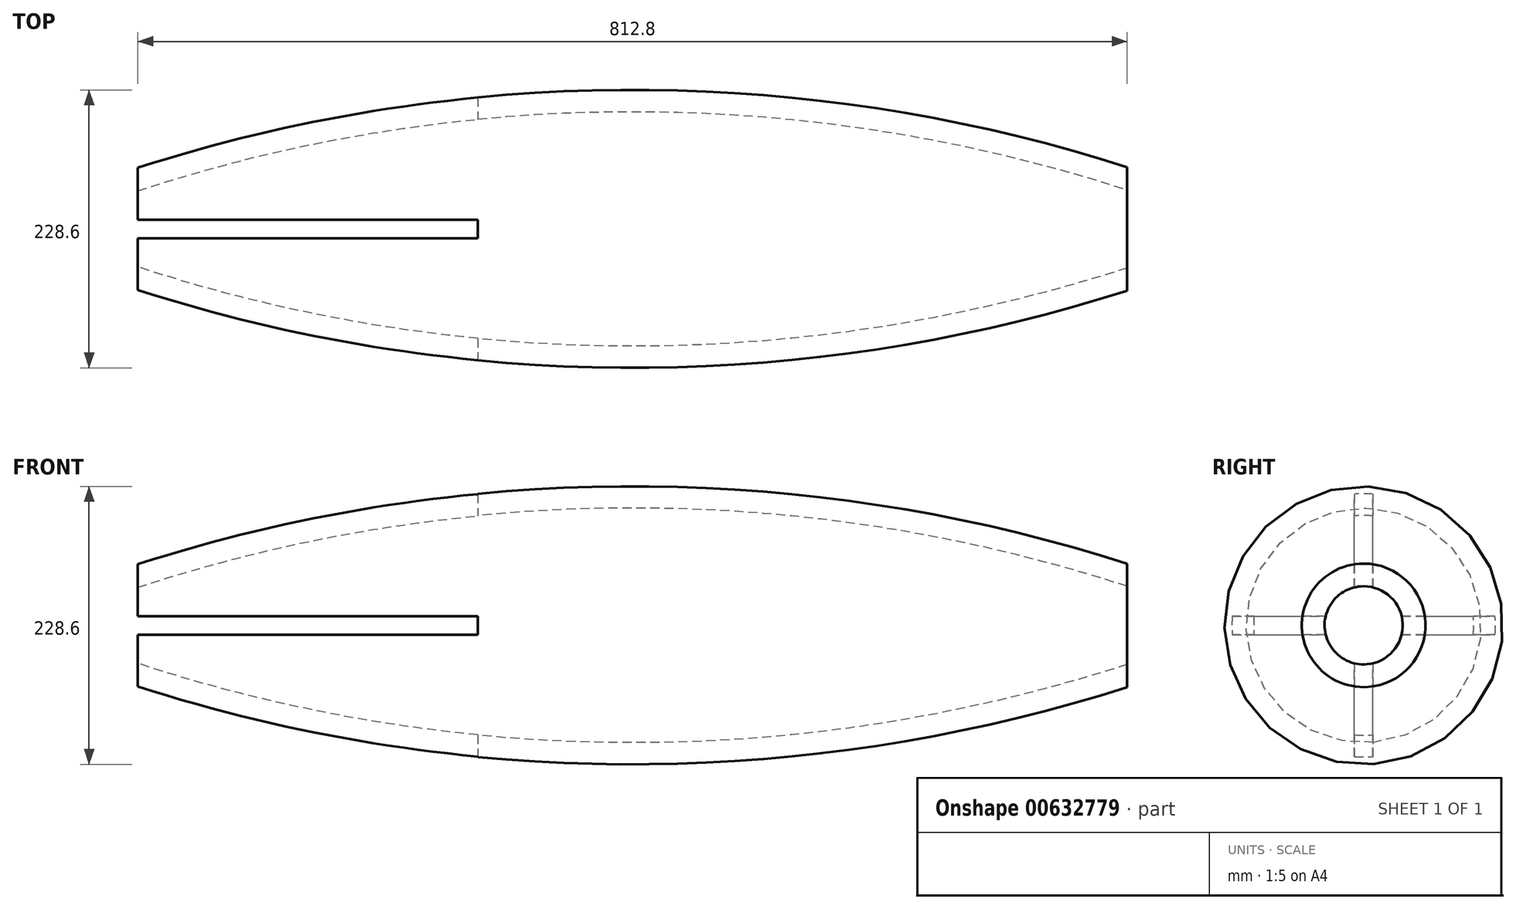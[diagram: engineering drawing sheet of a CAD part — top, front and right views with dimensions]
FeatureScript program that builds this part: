
annotation { "Feature Type Name" : "Feature", "Feature Type Description" : "" }
export const myFeature = defineFeature(function(context is Context, id is Id, definition is map)
    precondition{}
    {
        {
            var Q0;
            Q0=qCreatedBy(makeId("Front.planeOp"),FACE);
            var sketch = newSketch(context, id + "F0", { "sketchPlane" : qUnion([Q0])});
            skLineSegment(sketch, "E0", {"start": v(-406.4, 50.8) * mm, "end": v(-406.4, -50.8) * mm});
            skLineSegment(sketch, "E1", {"start": v(406.4, 50.8) * mm, "end": v(406.4, -50.8) * mm});
            skPoint(sketch, "E2.center.orphan", {"position": v(0, -206.92) * mm});
            skArc(sketch, "E3", {"start": v(406.4, 50.8) * mm, "mid": v(0, 114.3) * mm, "end": v(-406.4, 50.8) * mm});
            skArc(sketch, "E4", {"start": v(-406.4, -50.8) * mm, "mid": v(0, -114.3) * mm, "end": v(406.4, -50.8) * mm});
            skLineSegment(sketch, "E5", {"start": v(0, 114.3) * mm, "end": v(0, -114.3) * mm});
            skArc(sketch, "E6.0", {"start": v(406.4, 32.12) * mm, "mid": v(0, 96.52) * mm, "end": v(-406.4, 32.12) * mm});
            skLineSegment(sketch, "E7", {"start": v(-406.4, 0) * mm, "end": v(513.24, 0) * mm});
            skPoint(sketch, "E7.endSnap0", {"position": v(-406.4, 0) * mm});
            skSolve(sketch);
        }
        {
            var Q0;
            {var subQ0=sQuery(id+"F0.wireOp",EDGE,"E3");var subQ1=sQuery(id+"F0.wireOp",EDGE,"E1");var subQ2=makeQuery(id+"F0.imprint","INTERSECT",VERTEX,{"derivedFrom":[subQ1,subQ0]});Q0=makeQuery(id+"F0.imprint","IMPRINT",FACE,{"disambiguationData":[TD([[makeQuery(id+"F0.imprint","IMPRINT",EDGE,{"disambiguationData":[TD([[subQ2,-1.0]])],"derivedFrom":subQ1}),-1.0]])]});}
            var Q1;
            {var subQ0=sQuery(id+"F0.wireOp",EDGE,"E3");var subQ1=sQuery(id+"F0.wireOp",EDGE,"E0");var subQ2=makeQuery(id+"F0.imprint","INTERSECT",VERTEX,{"derivedFrom":[subQ1,subQ0]});Q1=makeQuery(id+"F0.imprint","IMPRINT",FACE,{"disambiguationData":[TD([[makeQuery(id+"F0.imprint","IMPRINT",EDGE,{"disambiguationData":[TD([[subQ2,-1.0]])],"derivedFrom":subQ1}),1.0]])]});}
            var Q2;
            Q2=sQuery(id+"F0.wireOp",EDGE,"E7");
            revolve(context, id + "F1", {"entities" : qUnion([Q0, Q1]), "axis" : qUnion([Q2]), "revolveType" : RevolveType.FULL});
        }
        {
            var Q0;
            Q0=makeQuery(id+"F1.opRevolve","SWEPT_FACE",FACE,{"disambiguationData":[OSD([sQuery(id+"F0.wireOp",EDGE,"E0")])]});
            var sketch = newSketch(context, id + "F2", { "sketchPlane" : qUnion([Q0])});
            skLineSegment(sketch, "E8.bottom", {"start": v(-127, 7.62) * mm, "end": v(127, 7.62) * mm});
            skLineSegment(sketch, "E8.top", {"start": v(-127, -7.62) * mm, "end": v(127, -7.62) * mm});
            skLineSegment(sketch, "E8.left", {"start": v(-127, 7.62) * mm, "end": v(-127, -7.62) * mm});
            skLineSegment(sketch, "E8.right", {"start": v(127, 7.62) * mm, "end": v(127, -7.62) * mm});
            skLineSegment(sketch, "E9.bottom", {"start": v(-7.62, 127) * mm, "end": v(7.62, 127) * mm});
            skLineSegment(sketch, "E9.top", {"start": v(-7.62, -127) * mm, "end": v(7.62, -127) * mm});
            skLineSegment(sketch, "E9.left", {"start": v(-7.62, 127) * mm, "end": v(-7.62, -127) * mm});
            skLineSegment(sketch, "E9.right", {"start": v(7.62, 127) * mm, "end": v(7.62, -127) * mm});
            skSolve(sketch);
        }
        {
            var Q0;
            {var subQ0=sQuery(id+"F2.wireOp",EDGE,"E9.left");var subQ1=sQuery(id+"F2.wireOp",EDGE,"E8.bottom");var subQ2=makeQuery(id+"F2.imprint","INTERSECT",VERTEX,{"derivedFrom":[subQ1,subQ0]});Q0=makeQuery(id+"F2.imprint","IMPRINT",FACE,{"disambiguationData":[TD([[makeQuery(id+"F2.imprint","IMPRINT",EDGE,{"disambiguationData":[TD([[subQ2,-1.0]])],"derivedFrom":subQ1}),1.0]])]});}
            var Q1;
            {var subQ0=sQuery(id+"F2.wireOp",EDGE,"E8.bottom");var subQ1=sQuery(id+"F0.wireOp",EDGE,"E0");var subQ2=makeQuery(id+"F1.opRevolve","SWEPT_EDGE",EDGE,{"disambiguationData":[OSD([subQ1,sQuery(id+"F0.wireOp",EDGE,"E3")])]});var subQ3=makeQuery(id+"F2.imprint","INTERSECT",VERTEX,{"disambiguationData":[OD(0.0)],"derivedFrom":[subQ2,subQ0]});Q1=makeQuery(id+"F2.imprint","IMPRINT",FACE,{"disambiguationData":[TD([[makeQuery(id+"F2.imprint","IMPRINT",EDGE,{"disambiguationData":[TD([[subQ3,-1.0]])],"derivedFrom":subQ0}),-1.0]])]});}
            var Q2;
            {var subQ0=sQuery(id+"F2.wireOp",EDGE,"E9.left");var subQ1=sQuery(id+"F0.wireOp",EDGE,"E0");var subQ2=makeQuery(id+"F1.opRevolve","SWEPT_EDGE",EDGE,{"disambiguationData":[OSD([subQ1,sQuery(id+"F0.wireOp",EDGE,"E3")])]});var subQ3=makeQuery(id+"F2.imprint","INTERSECT",VERTEX,{"disambiguationData":[OD(0.0)],"derivedFrom":[subQ2,subQ0]});Q2=makeQuery(id+"F2.imprint","IMPRINT",FACE,{"disambiguationData":[TD([[makeQuery(id+"F2.imprint","IMPRINT",EDGE,{"disambiguationData":[TD([[subQ3,-1.0]])],"derivedFrom":subQ0}),1.0]])]});}
            var Q3;
            {var subQ0=sQuery(id+"F2.wireOp",EDGE,"E9.top");Q3=makeQuery(id+"F2.imprint","IMPRINT",FACE,{"disambiguationData":[TD([[makeQuery(id+"F2.imprint","IMPRINT",EDGE,{"derivedFrom":subQ0}),1.0]])]});}
            var Q4;
            {var subQ0=sQuery(id+"F2.wireOp",EDGE,"E9.left");var subQ1=sQuery(id+"F2.wireOp",EDGE,"E8.top");var subQ2=makeQuery(id+"F2.imprint","INTERSECT",VERTEX,{"derivedFrom":[subQ1,subQ0]});Q4=makeQuery(id+"F2.imprint","IMPRINT",FACE,{"disambiguationData":[TD([[makeQuery(id+"F2.imprint","IMPRINT",EDGE,{"disambiguationData":[TD([[subQ2,-1.0]])],"derivedFrom":subQ1}),-1.0]])]});}
            var Q5;
            {var subQ0=sQuery(id+"F2.wireOp",EDGE,"E9.left");var subQ1=sQuery(id+"F0.wireOp",EDGE,"E0");var subQ2=makeQuery(id+"F1.opRevolve","SWEPT_EDGE",EDGE,{"disambiguationData":[OSD([subQ1,sQuery(id+"F0.wireOp",EDGE,"E3")])]});var subQ3=makeQuery(id+"F2.imprint","INTERSECT",VERTEX,{"disambiguationData":[OD(1.0)],"derivedFrom":[subQ2,subQ0]});Q5=makeQuery(id+"F2.imprint","IMPRINT",FACE,{"disambiguationData":[TD([[makeQuery(id+"F2.imprint","IMPRINT",EDGE,{"disambiguationData":[TD([[subQ3,1.0]])],"derivedFrom":subQ0}),1.0]])]});}
            var Q6;
            {var subQ0=sQuery(id+"F2.wireOp",EDGE,"E9.left");var subQ1=sQuery(id+"F2.wireOp",EDGE,"E8.bottom");var subQ2=makeQuery(id+"F2.imprint","INTERSECT",VERTEX,{"derivedFrom":[subQ1,subQ0]});Q6=makeQuery(id+"F2.imprint","IMPRINT",FACE,{"disambiguationData":[TD([[makeQuery(id+"F2.imprint","IMPRINT",EDGE,{"disambiguationData":[TD([[subQ2,-1.0]])],"derivedFrom":subQ1}),-1.0]])]});}
            var Q7;
            {var subQ0=sQuery(id+"F2.wireOp",EDGE,"E8.right");Q7=makeQuery(id+"F2.imprint","IMPRINT",FACE,{"disambiguationData":[TD([[makeQuery(id+"F2.imprint","IMPRINT",EDGE,{"derivedFrom":subQ0}),-1.0]])]});}
            var Q8;
            {var subQ0=sQuery(id+"F2.wireOp",EDGE,"E9.left");var subQ1=sQuery(id+"F2.wireOp",EDGE,"E8.bottom");var subQ2=makeQuery(id+"F2.imprint","INTERSECT",VERTEX,{"derivedFrom":[subQ1,subQ0]});Q8=makeQuery(id+"F2.imprint","IMPRINT",FACE,{"disambiguationData":[TD([[makeQuery(id+"F2.imprint","IMPRINT",EDGE,{"disambiguationData":[TD([[subQ2,-1.0]])],"derivedFrom":subQ0}),-1.0]])]});}
            var Q9;
            {var subQ0=sQuery(id+"F2.wireOp",EDGE,"E8.bottom");var subQ1=sQuery(id+"F0.wireOp",EDGE,"E0");var subQ2=makeQuery(id+"F1.opRevolve","SWEPT_EDGE",EDGE,{"disambiguationData":[OSD([subQ1,sQuery(id+"F0.wireOp",EDGE,"E3")])]});var subQ3=makeQuery(id+"F2.imprint","INTERSECT",VERTEX,{"disambiguationData":[OD(1.0)],"derivedFrom":[subQ2,subQ0]});Q9=makeQuery(id+"F2.imprint","IMPRINT",FACE,{"disambiguationData":[TD([[makeQuery(id+"F2.imprint","IMPRINT",EDGE,{"disambiguationData":[TD([[subQ3,1.0]])],"derivedFrom":subQ0}),-1.0]])]});}
            var Q10;
            {var subQ0=sQuery(id+"F2.wireOp",EDGE,"E9.right");var subQ1=sQuery(id+"F2.wireOp",EDGE,"E8.bottom");var subQ2=makeQuery(id+"F2.imprint","INTERSECT",VERTEX,{"derivedFrom":[subQ1,subQ0]});Q10=makeQuery(id+"F2.imprint","IMPRINT",FACE,{"disambiguationData":[TD([[makeQuery(id+"F2.imprint","IMPRINT",EDGE,{"disambiguationData":[TD([[subQ2,-1.0]])],"derivedFrom":subQ0}),1.0]])]});}
            var Q11;
            {var subQ0=sQuery(id+"F2.wireOp",EDGE,"E8.left");Q11=makeQuery(id+"F2.imprint","IMPRINT",FACE,{"disambiguationData":[TD([[makeQuery(id+"F2.imprint","IMPRINT",EDGE,{"derivedFrom":subQ0}),1.0]])]});}
            var Q12;
            {var subQ0=sQuery(id+"F2.wireOp",EDGE,"E9.bottom");Q12=makeQuery(id+"F2.imprint","IMPRINT",FACE,{"disambiguationData":[TD([[makeQuery(id+"F2.imprint","IMPRINT",EDGE,{"derivedFrom":subQ0}),-1.0]])]});}
            extrude(context, id + "F3", {"entities" : qUnion([Q0, Q1, Q2, Q3, Q4, Q5, Q6, Q7, Q8, Q9, Q10, Q11, Q12]), "operationType" : NewBodyOperationType.REMOVE, "oppositeDirection" : true, "depth" : 279.4 * mm, "offsetDistance" : 25.4 * mm});
        }
    });
